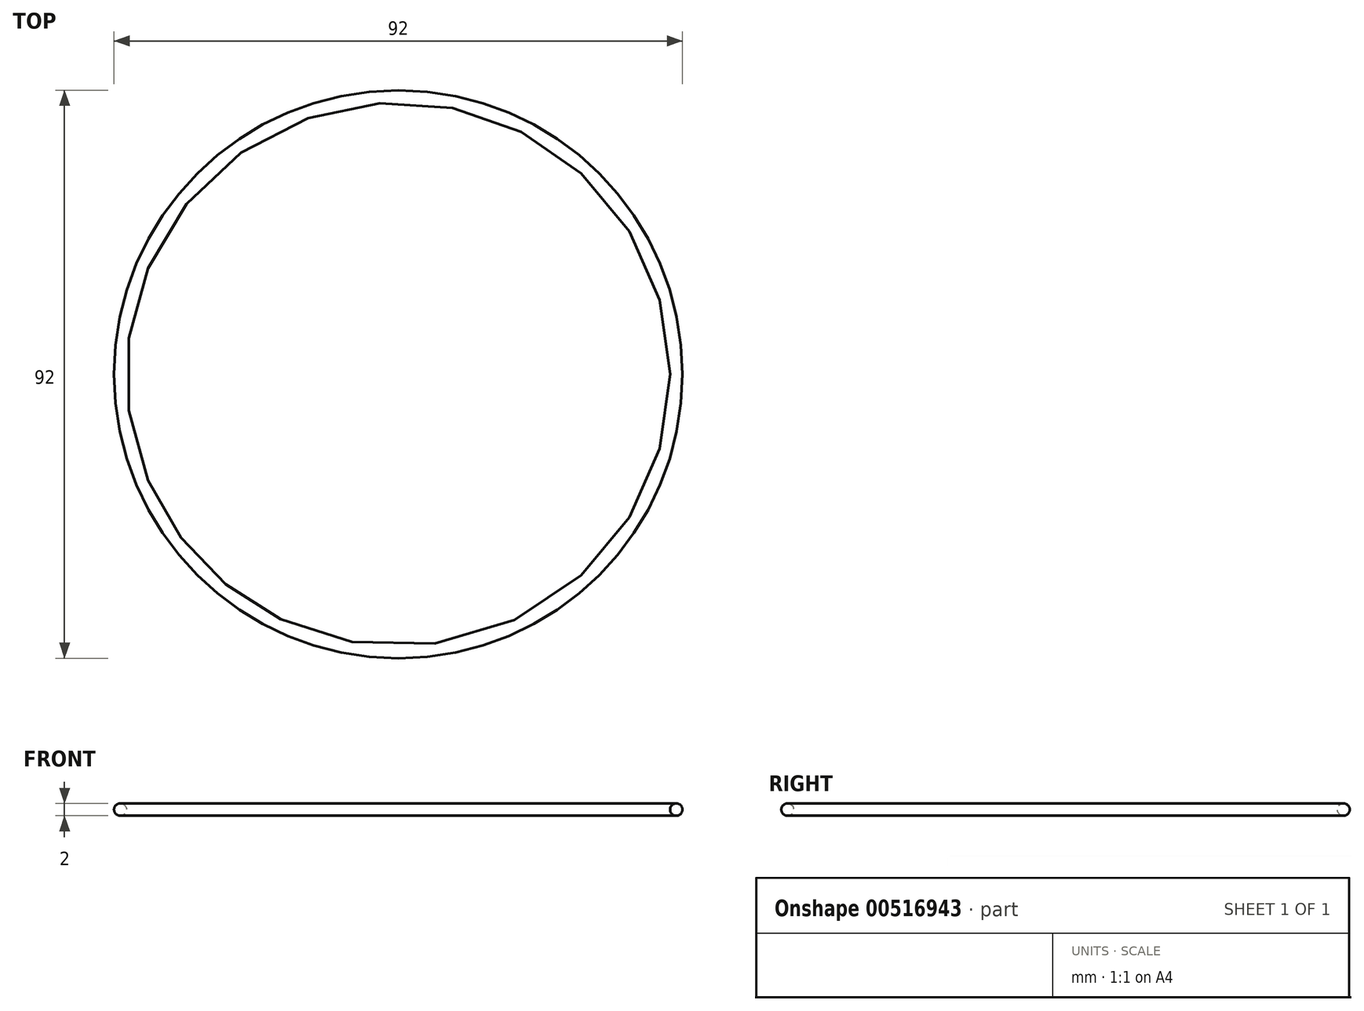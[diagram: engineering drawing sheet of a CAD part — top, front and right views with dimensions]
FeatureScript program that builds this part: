
annotation { "Feature Type Name" : "Feature", "Feature Type Description" : "" }
export const myFeature = defineFeature(function(context is Context, id is Id, definition is map)
    precondition{}
    {
        {
            var Q0;
            Q0=qCreatedBy(makeId("Front.planeOp"),FACE);
            var sketch = newSketch(context, id + "F0", { "sketchPlane" : qUnion([Q0])});
            skLineSegment(sketch, "E0", {"start": v(0, 0) * mm, "end": v(-45, 0) * mm});
            skPoint(sketch, "E1", {"position": v(-45, 0) * mm});
            skPoint(sketch, "E2", {"position": v(0, 0) * mm});
            skCircle(sketch, "E3", {"center": v(-45, 0) * mm, "radius": 1 * mm});
            skLineSegment(sketch, "E4", {"start": v(0, 0) * mm, "end": v(0, 20.27) * mm});
            skLineSegment(sketch, "E5", {"start": v(0, 20.27) * mm, "end": v(0, -24.37) * mm});
            skSolve(sketch);
        }
        {
            var Q0;
            Q0=makeQuery(id+"F0.imprint","IMPRINT",FACE,{"disambiguationData":[TD([[makeQuery(id+"F0.imprint","IMPRINT",EDGE,{"derivedFrom":sQuery(id+"F0.wireOp",EDGE,"E3")}),1.0]])]});
            var Q1;
            Q1=sQuery(id+"F0.wireOp",EDGE,"E5");
            revolve(context, id + "F1", {"entities" : qUnion([Q0]), "axis" : qUnion([Q1]), "revolveType" : RevolveType.FULL});
        }
    });
